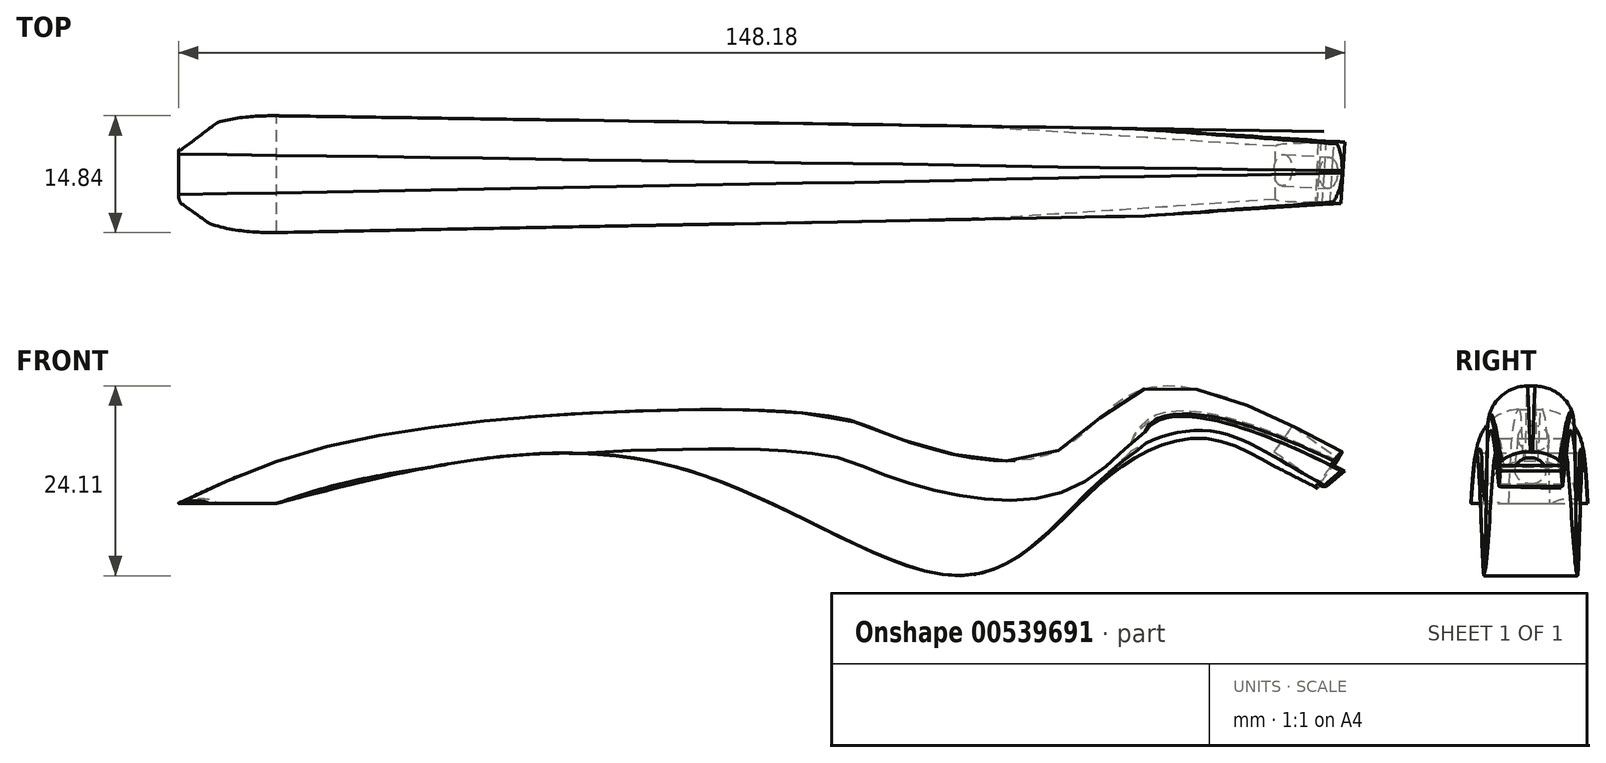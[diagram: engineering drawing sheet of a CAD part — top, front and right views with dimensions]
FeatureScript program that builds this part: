
annotation { "Feature Type Name" : "Feature", "Feature Type Description" : "" }
export const myFeature = defineFeature(function(context is Context, id is Id, definition is map)
    precondition{}
    {
        {
            var Q0;
            Q0=qCreatedBy(makeId("Front.planeOp"),FACE);
            var sketch = newSketch(context, id + "F0", { "sketchPlane" : qUnion([Q0])});
            skFitSpline(sketch, "E0", {"points": [v(-74.52, 0) * mm, v(-56.8, 6.91) * mm, v(-21.75, 11.48) * mm, v(9, 10.94) * mm, v(17.32, 8.12) * mm, v(36.25, 6.24) * mm, v(48.34, 14.57) * mm, v(84.73, 0) * mm], "startDerivative": vector(122.72, 57.7) * mm, "endDerivative": vector(227.18, -132.86) * mm});
            skLineSegment(sketch, "E1", {"start": v(84.73, 0) * mm, "end": v(81.5, -3.83) * mm});
            skLineSegment(sketch, "E2", {"start": v(81.5, -3.83) * mm, "end": v(64.85, 4.63) * mm});
            skFitSpline(sketch, "E3", {"points": [v(64.85, 4.63) * mm, v(56.8, 8.12) * mm, v(48.87, 6.78) * mm, v(39.88, 0) * mm, v(25.1, -9.2) * mm, v(-11.41, 4.63) * mm, v(-62.03, 0) * mm], "startDerivative": vector(-71.67, 41.24) * mm, "endDerivative": vector(-194.26, -50.08) * mm});
            skLineSegment(sketch, "E4", {"start": v(-62.03, 0) * mm, "end": v(-74.52, 0) * mm});
            skSolve(sketch);
        }
        {
            var Q0;
            Q0 = qSketchRegion(id + "F0", true);
            extrude(context, id + "F1", {"entities" : qUnion([Q0]), "depth" : 25 * mm, "offsetDistance" : 25 * mm});
        }
        {
            var Q0;
            Q0=qCreatedBy(makeId("Top.planeOp"),FACE);
            var sketch = newSketch(context, id + "F2", { "sketchPlane" : qUnion([Q0])});
            skLineSegment(sketch, "E5", {"start": v(86.01, -9.37) * mm, "end": v(-61.44, 0) * mm});
            skLineSegment(sketch, "E6", {"start": v(-61.44, 0) * mm, "end": v(-74.33, -9.67) * mm});
            skLineSegment(sketch, "E7", {"start": v(-74.33, -9.67) * mm, "end": v(-74.33, -16.26) * mm});
            skLineSegment(sketch, "E8", {"start": v(-74.33, -16.26) * mm, "end": v(-61.89, -25.1) * mm});
            skLineSegment(sketch, "E9", {"start": v(-61.89, -25.1) * mm, "end": v(86.16, -15.51) * mm});
            skLineSegment(sketch, "E10", {"start": v(86.16, -15.51) * mm, "end": v(86.16, -38) * mm});
            skLineSegment(sketch, "E11", {"start": v(86.16, -38) * mm, "end": v(-61.89, -25.1) * mm});
            skLineSegment(sketch, "E12", {"start": v(86.01, -9.37) * mm, "end": v(86.01, 10.7) * mm});
            skLineSegment(sketch, "E13", {"start": v(86.01, 10.7) * mm, "end": v(-61.44, 0) * mm});
            skLineSegment(sketch, "E14", {"start": v(-61.44, 0) * mm, "end": v(-66.08, 13.1) * mm});
            skLineSegment(sketch, "E15", {"start": v(-66.08, 13.1) * mm, "end": v(-79.75, 2.85) * mm});
            skLineSegment(sketch, "E16", {"start": v(-79.75, 2.85) * mm, "end": v(-74.33, -9.67) * mm});
            skLineSegment(sketch, "E17", {"start": v(-74.33, -16.26) * mm, "end": v(-80.77, -22.26) * mm});
            skLineSegment(sketch, "E18", {"start": v(-80.77, -22.26) * mm, "end": v(-72.44, -33.36) * mm});
            skLineSegment(sketch, "E19", {"start": v(-72.44, -33.36) * mm, "end": v(-61.89, -25.1) * mm});
            skSolve(sketch);
        }
        {
            var Q0;
            Q0 = qSketchRegion(id + "F2", true);
            extrude(context, id + "F3", {"entities" : qUnion([Q0]), "operationType" : NewBodyOperationType.REMOVE, "endBound" : BoundingType.SYMMETRIC, "oppositeDirection" : true, "depth" : 64.5 * mm, "offsetDistance" : 25 * mm});
        }
        {
            var Q0;
            Q0=qCreatedBy(makeId("Top.planeOp"),FACE);
            var sketch = newSketch(context, id + "F4", { "sketchPlane" : qUnion([Q0])});
            skLineSegment(sketch, "E20", {"start": v(48.35, -6.88) * mm, "end": v(-77.82, -5) * mm});
            skLineSegment(sketch, "E21", {"start": v(-77.82, -5) * mm, "end": v(-78.04, -20.37) * mm});
            skLineSegment(sketch, "E22", {"start": v(-78.04, -20.37) * mm, "end": v(48.5, -17.96) * mm});
            skLineSegment(sketch, "E23", {"start": v(48.5, -17.96) * mm, "end": v(41.6, -43.34) * mm});
            skLineSegment(sketch, "E24", {"start": v(41.6, -43.34) * mm, "end": v(-78.04, -27.28) * mm});
            skLineSegment(sketch, "E25", {"start": v(-78.04, -27.28) * mm, "end": v(-78.04, -20.37) * mm});
            skLineSegment(sketch, "E26", {"start": v(48.35, -6.88) * mm, "end": v(39.35, 36.32) * mm});
            skLineSegment(sketch, "E27", {"start": v(39.35, 36.32) * mm, "end": v(-77.82, -5) * mm});
            skSolve(sketch);
        }
        {
            var Q0;
            Q0 = qSketchRegion(id + "F4", true);
            extrude(context, id + "F5", {"entities" : qUnion([Q0]), "operationType" : NewBodyOperationType.REMOVE, "endBound" : BoundingType.SYMMETRIC, "oppositeDirection" : true, "depth" : 109 * mm, "offsetDistance" : 25 * mm});
        }
        {
            var Q0;
            Q0=makeQuery(id+"F5.boolean.opBoolean","INTERSECT",EDGE,{"derivedFrom":[makeQuery(id+"F1.opExtrude","SWEPT_FACE",FACE,{"disambiguationData":[OSD([sQuery(id+"F0.wireOp",EDGE,"E0")])]}),makeQuery(id+"F5.opExtrude","SWEPT_FACE",FACE,{"disambiguationData":[OSD([sQuery(id+"F4.wireOp",EDGE,"E20")])]})]});
            var Q1;
            Q1=makeQuery(id+"F5.boolean.opBoolean","INTERSECT",EDGE,{"derivedFrom":[makeQuery(id+"F1.opExtrude","SWEPT_FACE",FACE,{"disambiguationData":[OSD([sQuery(id+"F0.wireOp",EDGE,"E0")])]}),makeQuery(id+"F5.opExtrude","SWEPT_FACE",FACE,{"disambiguationData":[OSD([sQuery(id+"F4.wireOp",EDGE,"E22")])]})]});
            fillet(context, id + "F6", {"entities" : qUnion([Q0, Q1]), "radius" : 5 * mm, "tangentPropagation" : true, "allowEdgeOverflow" : false});
        }
        {
            var Q0;
            Q0=makeQuery(id+"F5.boolean.opBoolean","INTERSECT",EDGE,{"derivedFrom":[makeQuery(id+"F1.opExtrude","SWEPT_FACE",FACE,{"disambiguationData":[OSD([sQuery(id+"F0.wireOp",EDGE,"E3")])]}),makeQuery(id+"F5.opExtrude","SWEPT_FACE",FACE,{"disambiguationData":[OSD([sQuery(id+"F4.wireOp",EDGE,"E20")])]})]});
            var Q1;
            Q1=makeQuery(id+"F5.boolean.opBoolean","INTERSECT",EDGE,{"derivedFrom":[makeQuery(id+"F1.opExtrude","SWEPT_FACE",FACE,{"disambiguationData":[OSD([sQuery(id+"F0.wireOp",EDGE,"E3")])]}),makeQuery(id+"F5.opExtrude","SWEPT_FACE",FACE,{"disambiguationData":[OSD([sQuery(id+"F4.wireOp",EDGE,"E22")])]})]});
            fillet(context, id + "F7", {"entities" : qUnion([Q0, Q1]), "radius" : 0.02 * mm, "tangentPropagation" : true, "allowEdgeOverflow" : false});
        }
        {
            var Q0;
            Q0=makeQuery(id+"F3.boolean.opBoolean","INTERSECT",EDGE,{"derivedFrom":[makeQuery(id+"F1.opExtrude","SWEPT_FACE",FACE,{"disambiguationData":[OSD([sQuery(id+"F0.wireOp",EDGE,"E3")])]}),makeQuery(id+"F3.opExtrude","SWEPT_FACE",FACE,{"disambiguationData":[OSD([sQuery(id+"F2.wireOp",EDGE,"E5")])]})]});
            var Q1;
            Q1=makeQuery(id+"F3.boolean.opBoolean","INTERSECT",EDGE,{"derivedFrom":[makeQuery(id+"F1.opExtrude","SWEPT_FACE",FACE,{"disambiguationData":[OSD([sQuery(id+"F0.wireOp",EDGE,"E3")])]}),makeQuery(id+"F3.opExtrude","SWEPT_FACE",FACE,{"disambiguationData":[OSD([sQuery(id+"F2.wireOp",EDGE,"E9")])]})]});
            fillet(context, id + "F8", {"entities" : qUnion([Q0, Q1]), "radius" : 1 * mm, "tangentPropagation" : true, "allowEdgeOverflow" : false});
        }
        {
            var Q0;
            Q0=qCreatedBy(makeId("Top.planeOp"),FACE);
            var sketch = newSketch(context, id + "F9", { "sketchPlane" : qUnion([Q0])});
            skLineSegment(sketch, "E28.bottom", {"start": v(90.12, -1.95) * mm, "end": v(75.09, -1.95) * mm});
            skLineSegment(sketch, "E28.top", {"start": v(90.12, -27.73) * mm, "end": v(75.09, -27.73) * mm});
            skLineSegment(sketch, "E28.left", {"start": v(90.12, -1.95) * mm, "end": v(90.12, -27.73) * mm});
            skLineSegment(sketch, "E28.right", {"start": v(75.09, -1.95) * mm, "end": v(75.09, -27.73) * mm});
            skSolve(sketch);
        }
        {
            var Q0;
            Q0 = qSketchRegion(id + "F9", true);
            extrude(context, id + "F10", {"entities" : qUnion([Q0]), "operationType" : NewBodyOperationType.REMOVE, "endBound" : BoundingType.SYMMETRIC, "oppositeDirection" : true, "depth" : 36.2 * mm, "offsetDistance" : 25 * mm});
        }
        {
            var Q0;
            Q0=makeQuery(id+"F3.boolean.opBoolean","COPY",FACE,{"derivedFrom":makeQuery(id+"F3.opExtrude","SWEPT_FACE",FACE,{"disambiguationData":[OSD([sQuery(id+"F2.wireOp",EDGE,"E5")])]})});
            var sketch = newSketch(context, id + "F11", { "sketchPlane" : qUnion([Q0])});
            skLineSegment(sketch, "E29", {"start": v(-75.5, 5.3) * mm, "end": v(-69.18, 0) * mm});
            skLineSegment(sketch, "E30", {"start": v(-69.18, 0) * mm, "end": v(-75.49, -3.83) * mm});
            skLineSegment(sketch, "E31", {"start": v(-75.49, -3.83) * mm, "end": v(-83.7, -0.07) * mm});
            skLineSegment(sketch, "E32", {"start": v(-83.7, -0.07) * mm, "end": v(-75.5, 5.3) * mm});
            skSolve(sketch);
        }
        {
            var Q0;
            Q0 = qSketchRegion(id + "F11", true);
            extrude(context, id + "F12", {"entities" : qUnion([Q0]), "operationType" : NewBodyOperationType.REMOVE, "oppositeDirection" : true, "depth" : 25 * mm, "offsetDistance" : 25 * mm});
        }
        {
            var Q0;
            Q0=makeQuery(id+"F3.boolean.opBoolean","COPY",FACE,{"derivedFrom":makeQuery(id+"F3.opExtrude","SWEPT_FACE",FACE,{"disambiguationData":[OSD([sQuery(id+"F2.wireOp",EDGE,"E5")])]})});
            var sketch = newSketch(context, id + "F13", { "sketchPlane" : qUnion([Q0])});
            skLineSegment(sketch, "E33", {"start": v(-73.89, 6.51) * mm, "end": v(-69.31, 0) * mm});
            skLineSegment(sketch, "E34", {"start": v(-69.31, 0) * mm, "end": v(-80.34, 0) * mm});
            skLineSegment(sketch, "E35", {"start": v(-80.34, 0) * mm, "end": v(-79, 8.26) * mm});
            skLineSegment(sketch, "E36", {"start": v(-79, 8.26) * mm, "end": v(-73.89, 6.51) * mm});
            skSolve(sketch);
        }
        {
            var Q0;
            {var subQ8=makeQuery(id+"F12.boolean.opBoolean","COPY",EDGE,{"derivedFrom":makeQuery(id+"F12.opExtrude","CAP_EDGE",EDGE,{"disambiguationData":[OSD([sQuery(id+"F11.wireOp",EDGE,"E29")])],"isStart":true})});Q0=makeQuery(id+"F13.imprint","IMPRINT",FACE,{"disambiguationData":[TD([[makeQuery(id+"F13.imprint","IMPRINT",EDGE,{"derivedFrom":subQ8}),1.0]])]});}
            var Q1;
            {var subQ0=sQuery(id+"F13.wireOp",EDGE,"E34");Q1=makeQuery(id+"F13.imprint","IMPRINT",FACE,{"disambiguationData":[TD([[makeQuery(id+"F13.imprint","IMPRINT",EDGE,{"derivedFrom":subQ0}),-1.0]])]});}
            var Q2;
            Q2=sQuery(id+"F13.wireOp",EDGE,"E33");
            var Q3;
            Q3=sQuery(id+"F13.wireOp",EDGE,"E36");
            var Q4;
            Q4=sQuery(id+"F13.wireOp",EDGE,"E35");
            var Q5;
            Q5=sQuery(id+"F13.wireOp",EDGE,"E34");
            extrude(context, id + "F14", {"entities" : qUnion([Q0, Q1]), "operationType" : NewBodyOperationType.REMOVE, "surfaceEntities" : qUnion([Q2, Q3, Q4, Q5]), "oppositeDirection" : true, "depth" : 25 * mm, "offsetDistance" : 25 * mm});
        }
        {
            var Q0;
            Q0=makeQuery(id+"F14.boolean.opBoolean","COPY",FACE,{"derivedFrom":makeQuery(id+"F14.opExtrude","SWEPT_FACE",FACE,{"disambiguationData":[OSD([sQuery(id+"F13.wireOp",EDGE,"E33")])]})});
            var sketch = newSketch(context, id + "F15", { "sketchPlane" : qUnion([Q0])});
            skCircle(sketch, "E37", {"center": v(-9.58, 44.59) * mm, "radius": 2 * mm});
            skSolve(sketch);
        }
        {
            var Q0;
            Q0 = qSketchRegion(id + "F15", true);
            extrude(context, id + "F16", {"entities" : qUnion([Q0]), "operationType" : NewBodyOperationType.REMOVE, "oppositeDirection" : true, "depth" : 7.1 * mm, "offsetDistance" : 25 * mm});
        }
    });
